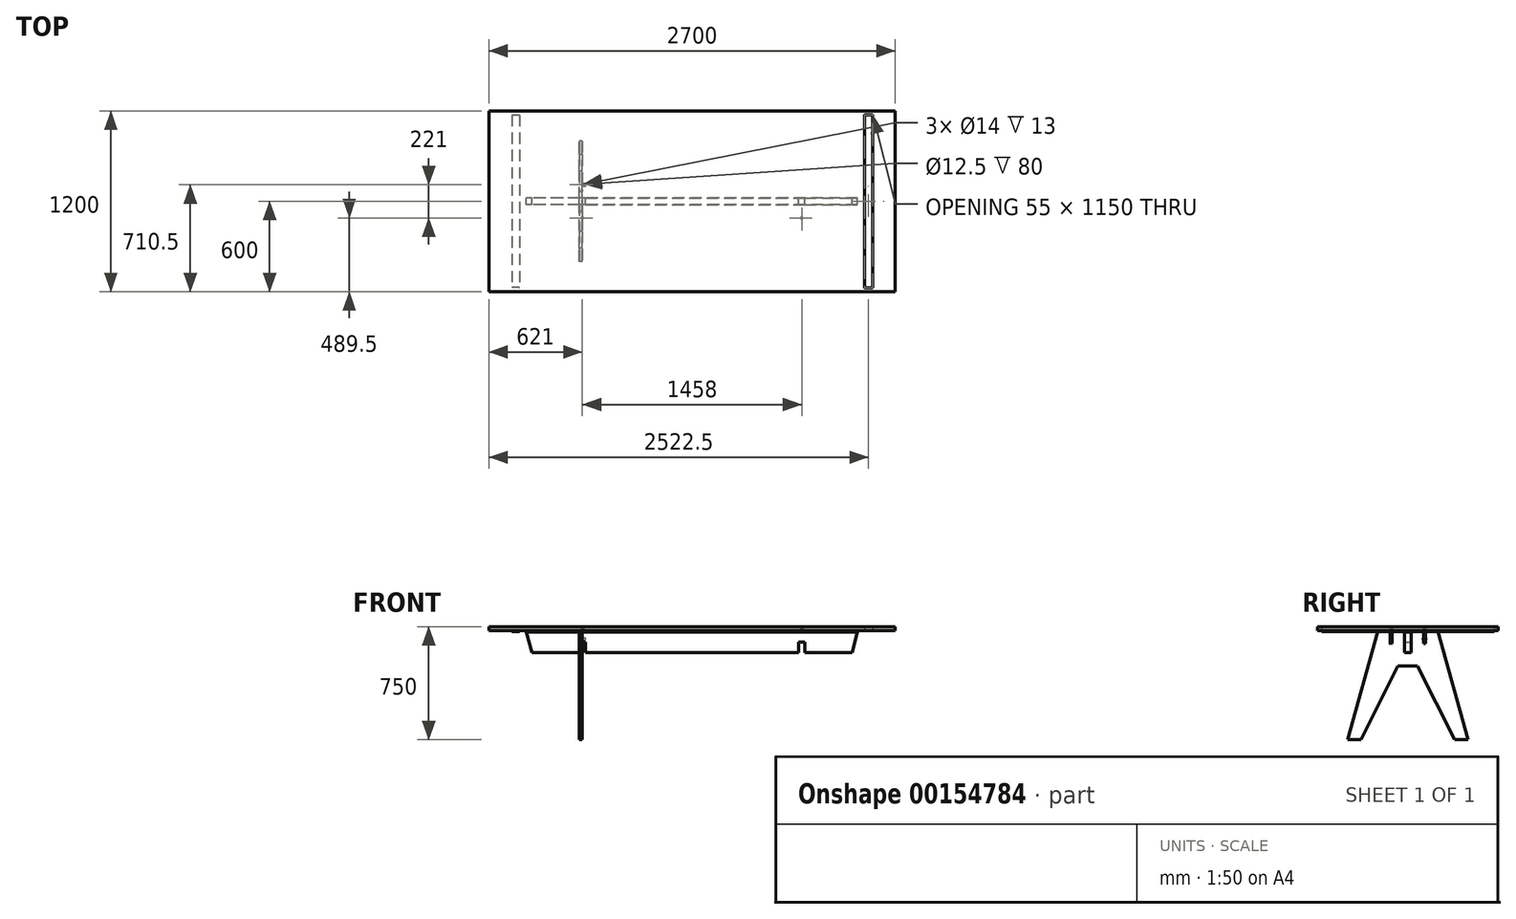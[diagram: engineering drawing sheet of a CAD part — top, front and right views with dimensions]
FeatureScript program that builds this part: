
annotation { "Feature Type Name" : "Feature", "Feature Type Description" : "" }
export const myFeature = defineFeature(function(context is Context, id is Id, definition is map)
    precondition{}
    {
        {
            var Q0;
            Q0=qCreatedBy(makeId("Top.planeOp"),FACE);
            var sketch = newSketch(context, id + "F0", { "sketchPlane" : qUnion([Q0])});
            skLineSegment(sketch, "E0.bottom", {"start": v(1350, 600) * mm, "end": v(-1350, 600) * mm});
            skLineSegment(sketch, "E0.top", {"start": v(1350, -600) * mm, "end": v(-1350, -600) * mm});
            skLineSegment(sketch, "E0.left", {"start": v(1350, 600) * mm, "end": v(1350, -600) * mm});
            skLineSegment(sketch, "E0.right", {"start": v(-1350, 600) * mm, "end": v(-1350, -600) * mm});
            skPoint(sketch, "E0.middle", {"position": v(0, 0) * mm});
            skLineSegment(sketch, "E1.bottom", {"start": v(-1148, 575) * mm, "end": v(-1197, 575) * mm});
            skLineSegment(sketch, "E1.top", {"start": v(-1148, -575) * mm, "end": v(-1197, -575) * mm});
            skLineSegment(sketch, "E1.left", {"start": v(-1145, 572) * mm, "end": v(-1145, -572) * mm});
            skLineSegment(sketch, "E1.right", {"start": v(-1200, 572) * mm, "end": v(-1200, -572) * mm});
            skPoint(sketch, "E1.middle", {"position": v(-1172.5, 0) * mm});
            skPoint(sketch, "E2.visualSharp", {"position": v(-1200, 575) * mm});
            skArc(sketch, "E2.filletArc", {"start": v(-1197, 575) * mm, "mid": v(-1199.12, 574.12) * mm, "end": v(-1200, 572) * mm});
            skPoint(sketch, "E3.visualSharp", {"position": v(-1145, 575) * mm});
            skArc(sketch, "E3.filletArc", {"start": v(-1145, 572) * mm, "mid": v(-1145.88, 574.12) * mm, "end": v(-1148, 575) * mm});
            skPoint(sketch, "E4.visualSharp", {"position": v(-1200, -575) * mm});
            skArc(sketch, "E4.filletArc", {"start": v(-1200, -572) * mm, "mid": v(-1199.12, -574.12) * mm, "end": v(-1197, -575) * mm});
            skPoint(sketch, "E5.visualSharp", {"position": v(-1145, -575) * mm});
            skArc(sketch, "E5.filletArc", {"start": v(-1148, -575) * mm, "mid": v(-1145.88, -574.12) * mm, "end": v(-1145, -572) * mm});
            skArc(sketch, "E6.MirrorCS", {"start": v(1148, -575) * mm, "mid": v(1145.88, -574.12) * mm, "end": v(1145, -572) * mm});
            skLineSegment(sketch, "E7.MirrorCS", {"start": v(1148, -575) * mm, "end": v(1197, -575) * mm});
            skArc(sketch, "E8.MirrorCS", {"start": v(1200, -572) * mm, "mid": v(1199.12, -574.12) * mm, "end": v(1197, -575) * mm});
            skLineSegment(sketch, "E9.MirrorCS", {"start": v(1148, 575) * mm, "end": v(1197, 575) * mm});
            skArc(sketch, "E10.MirrorCS", {"start": v(1197, 575) * mm, "mid": v(1199.12, 574.12) * mm, "end": v(1200, 572) * mm});
            skArc(sketch, "E11.MirrorCS", {"start": v(1145, 572) * mm, "mid": v(1145.88, 574.12) * mm, "end": v(1148, 575) * mm});
            skPoint(sketch, "E12.MirrorP", {"position": v(1172.5, 0) * mm});
            skLineSegment(sketch, "E13.MirrorCS", {"start": v(1145, 572) * mm, "end": v(1145, -572) * mm});
            skPoint(sketch, "E14.MirrorP", {"position": v(1145, -575) * mm});
            skLineSegment(sketch, "E15.MirrorCS", {"start": v(1200, 572) * mm, "end": v(1200, -572) * mm});
            skPoint(sketch, "E16.MirrorP", {"position": v(1200, -575) * mm});
            skArc(sketch, "E17.0", {"start": v(-1147.5, 572) * mm, "mid": v(-1147.65, 572.35) * mm, "end": v(-1148, 572.5) * mm});
            skLineSegment(sketch, "E17.1", {"start": v(-1148, 572.5) * mm, "end": v(-1197, 572.5) * mm});
            skLineSegment(sketch, "E17.2", {"start": v(-1147.5, 572) * mm, "end": v(-1147.5, -572) * mm});
            skArc(sketch, "E17.3", {"start": v(-1197, 572.5) * mm, "mid": v(-1197.35, 572.35) * mm, "end": v(-1197.5, 572) * mm});
            skArc(sketch, "E17.4", {"start": v(-1148, -572.5) * mm, "mid": v(-1147.65, -572.35) * mm, "end": v(-1147.5, -572) * mm});
            skLineSegment(sketch, "E17.5", {"start": v(-1148, -572.5) * mm, "end": v(-1197, -572.5) * mm});
            skArc(sketch, "E17.6", {"start": v(-1197.5, -572) * mm, "mid": v(-1197.35, -572.35) * mm, "end": v(-1197, -572.5) * mm});
            skLineSegment(sketch, "E17.7", {"start": v(-1197.5, 572) * mm, "end": v(-1197.5, -572) * mm});
            skSolve(sketch);
        }
        {
            var Q0;
            Q0=makeQuery(id+"F0.imprint","IMPRINT",FACE,{"disambiguationData":[TD([[makeQuery(id+"F0.imprint","IMPRINT",EDGE,{"derivedFrom":sQuery(id+"F0.wireOp",EDGE,"E1.bottom")}),1.0]])]});
            var Q1;
            Q1=makeQuery(id+"F0.imprint","IMPRINT",FACE,{"disambiguationData":[TD([[makeQuery(id+"F0.imprint","IMPRINT",EDGE,{"derivedFrom":sQuery(id+"F0.wireOp",EDGE,"E6.MirrorCS")}),-1.0]])]});
            var Q2;
            Q2=makeQuery(id+"F0.imprint","IMPRINT",FACE,{"disambiguationData":[TD([[makeQuery(id+"F0.imprint","IMPRINT",EDGE,{"derivedFrom":sQuery(id+"F0.wireOp",EDGE,"E0.bottom")}),1.0]])]});
            var Q3;
            Q3=makeQuery(id+"F0.imprint","IMPRINT",FACE,{"disambiguationData":[TD([[makeQuery(id+"F0.imprint","IMPRINT",EDGE,{"derivedFrom":sQuery(id+"F0.wireOp",EDGE,"E17.0")}),1.0]])]});
            extrude(context, id + "F1", {"entities" : qUnion([Q0, Q1, Q2, Q3]), "depth" : 32 * mm});
        }
        {
            var Q0;
            Q0=makeQuery(id+"F0.imprint","IMPRINT",FACE,{"disambiguationData":[TD([[makeQuery(id+"F0.imprint","IMPRINT",EDGE,{"derivedFrom":sQuery(id+"F0.wireOp",EDGE,"E1.bottom")}),1.0]])]});
            var Q1;
            Q1=makeQuery(id+"F0.imprint","IMPRINT",FACE,{"disambiguationData":[TD([[makeQuery(id+"F0.imprint","IMPRINT",EDGE,{"derivedFrom":sQuery(id+"F0.wireOp",EDGE,"E6.MirrorCS")}),-1.0]])]});
            var Q2;
            Q2=makeQuery(id+"F0.imprint","IMPRINT",FACE,{"disambiguationData":[TD([[makeQuery(id+"F0.imprint","IMPRINT",EDGE,{"derivedFrom":sQuery(id+"F0.wireOp",EDGE,"E17.0")}),1.0]])]});
            extrude(context, id + "F2", {"entities" : qUnion([Q0, Q1, Q2]), "operationType" : NewBodyOperationType.REMOVE, "depth" : 5 * mm});
        }
        {
            var Q0;
            Q0=makeQuery(id+"F0.imprint","IMPRINT",FACE,{"disambiguationData":[TD([[makeQuery(id+"F0.imprint","IMPRINT",EDGE,{"derivedFrom":sQuery(id+"F0.wireOp",EDGE,"E17.0")}),1.0]])]});
            extrude(context, id + "F3", {"entities" : qUnion([Q0]), "depth" : 5 * mm});
        }
        {
            var Q0;
            Q0=qCreatedBy(makeId("Right.planeOp"),FACE);
            cPlane(context, id + "F4", {"entities" : qUnion([Q0]), "cplaneType" : CPlaneType.OFFSET, "offset" : 750 * mm, "oppositeDirection" : true, "width" : 150 * mm, "height" : 150 * mm});
        }
        {
            var Q0;
            Q0=qCreatedBy(id+"F4.planeOp",FACE);
            var sketch = newSketch(context, id + "F5", { "sketchPlane" : qUnion([Q0])});
            skLineSegment(sketch, "E18", {"start": v(0, 0) * mm, "end": v(-200, 0) * mm});
            skLineSegment(sketch, "E19", {"start": v(-200, 0) * mm, "end": v(-400, -718) * mm});
            skLineSegment(sketch, "E20", {"start": v(-400, -718) * mm, "end": v(-310, -718) * mm});
            skLineSegment(sketch, "E21", {"start": v(-65, -228) * mm, "end": v(0, -228) * mm});
            skLineSegment(sketch, "E22.MirrorCS", {"start": v(400, -718) * mm, "end": v(310, -718) * mm});
            skLineSegment(sketch, "E23.MirrorCS", {"start": v(200, 0) * mm, "end": v(400, -718) * mm});
            skLineSegment(sketch, "E24.MirrorCS", {"start": v(0, 0) * mm, "end": v(200, 0) * mm});
            skLineSegment(sketch, "E25.bottom", {"start": v(-21, 0) * mm, "end": v(21, 0) * mm});
            skLineSegment(sketch, "E25.top", {"start": v(-21, -140) * mm, "end": v(21, -140) * mm});
            skLineSegment(sketch, "E25.left", {"start": v(-21, 0) * mm, "end": v(-21, -140) * mm});
            skLineSegment(sketch, "E25.right", {"start": v(21, 0) * mm, "end": v(21, -140) * mm});
            skPoint(sketch, "E25.middle", {"position": v(0, -70) * mm});
            skLineSegment(sketch, "E26", {"start": v(-310, -718) * mm, "end": v(-65, -228) * mm});
            skLineSegment(sketch, "E27.MirrorCS", {"start": v(310, -718) * mm, "end": v(65, -228) * mm});
            skLineSegment(sketch, "E28.MirrorCS", {"start": v(65, -228) * mm, "end": v(0, -228) * mm});
            skLineSegment(sketch, "E29", {"start": v(21, -70) * mm, "end": v(-21, -70) * mm});
            skSolve(sketch);
        }
        {
            var Q0;
            {var subQ5=sQuery(id+"F5.wireOp",EDGE,"E18");Q0=makeQuery(id+"F5.imprint","IMPRINT",FACE,{"disambiguationData":[TD([[makeQuery(id+"F5.imprint","IMPRINT",EDGE,{"derivedFrom":subQ5}),1.0]])]});}
            var Q1;
            {var subQ0=sQuery(id+"F5.wireOp",EDGE,"E25.top");Q1=makeQuery(id+"F5.imprint","IMPRINT",FACE,{"disambiguationData":[TD([[makeQuery(id+"F5.imprint","IMPRINT",EDGE,{"derivedFrom":subQ0}),1.0]])]});}
            extrude(context, id + "F6", {"entities" : qUnion([Q0, Q1]), "depth" : 42 * mm});
        }
        {
            var Q0;
            Q0=makeQuery(id+"F6.opExtrude","SWEPT_FACE",FACE,{"disambiguationData":[OSD([sQuery(id+"F5.wireOp",EDGE,"E24.MirrorCS")])]});
            var sketch = newSketch(context, id + "F7", { "sketchPlane" : qUnion([Q0])});
            skCircle(sketch, "E30", {"center": v(-729, 110.5) * mm, "radius": 7 * mm});
            skPoint(sketch, "E30.centerSnap0", {"position": v(-729, 200) * mm});
            skPoint(sketch, "E30.centerSnap1", {"position": v(-708, 110.5) * mm});
            skCircle(sketch, "E31", {"center": v(-729, 110.5) * mm, "radius": 6.25 * mm});
            skCircle(sketch, "E32.MirrorC", {"center": v(-729, -110.5) * mm, "radius": 7 * mm});
            skCircle(sketch, "E33.MirrorC", {"center": v(-729, -110.5) * mm, "radius": 6.25 * mm});
            skCircle(sketch, "E34.MirrorC", {"center": v(729, 110.5) * mm, "radius": 7 * mm});
            skCircle(sketch, "E35.MirrorC", {"center": v(729, -110.5) * mm, "radius": 7 * mm});
            skSolve(sketch);
        }
        {
            var Q0;
            Q0=makeQuery(id+"F7.imprint","IMPRINT",FACE,{"disambiguationData":[TD([[makeQuery(id+"F7.imprint","IMPRINT",EDGE,{"derivedFrom":sQuery(id+"F7.wireOp",EDGE,"E30")}),1.0]])]});
            var Q1;
            Q1=makeQuery(id+"F7.imprint","IMPRINT",FACE,{"disambiguationData":[TD([[makeQuery(id+"F7.imprint","IMPRINT",EDGE,{"derivedFrom":sQuery(id+"F7.wireOp",EDGE,"E31")}),1.0]])]});
            var Q2;
            Q2=makeQuery(id+"F7.imprint","IMPRINT",FACE,{"disambiguationData":[TD([[makeQuery(id+"F7.imprint","IMPRINT",EDGE,{"derivedFrom":sQuery(id+"F7.wireOp",EDGE,"E32.MirrorC")}),-1.0]])]});
            var Q3;
            Q3=makeQuery(id+"F7.imprint","IMPRINT",FACE,{"disambiguationData":[TD([[makeQuery(id+"F7.imprint","IMPRINT",EDGE,{"derivedFrom":sQuery(id+"F7.wireOp",EDGE,"E33.MirrorC")}),-1.0]])]});
            var Q4;
            Q4=makeQuery(id+"F7.imprint","IMPRINT",FACE,{"disambiguationData":[TD([[makeQuery(id+"F7.imprint","IMPRINT",EDGE,{"derivedFrom":sQuery(id+"F7.wireOp",EDGE,"E35.MirrorC")}),1.0]])]});
            var Q5;
            Q5=makeQuery(id+"F7.imprint","IMPRINT",FACE,{"disambiguationData":[TD([[makeQuery(id+"F7.imprint","IMPRINT",EDGE,{"derivedFrom":sQuery(id+"F7.wireOp",EDGE,"E34.MirrorC")}),-1.0]])]});
            extrude(context, id + "F8", {"entities" : qUnion([Q0, Q1, Q2, Q3, Q4, Q5]), "operationType" : NewBodyOperationType.REMOVE, "depth" : 18 * mm});
        }
        {
            var Q0;
            Q0=makeQuery(id+"F7.imprint","IMPRINT",FACE,{"disambiguationData":[TD([[makeQuery(id+"F7.imprint","IMPRINT",EDGE,{"derivedFrom":sQuery(id+"F7.wireOp",EDGE,"E31")}),1.0]])]});
            var Q1;
            Q1=makeQuery(id+"F7.imprint","IMPRINT",FACE,{"disambiguationData":[TD([[makeQuery(id+"F7.imprint","IMPRINT",EDGE,{"derivedFrom":sQuery(id+"F7.wireOp",EDGE,"E33.MirrorC")}),-1.0]])]});
            extrude(context, id + "F9", {"entities" : qUnion([Q0, Q1]), "operationType" : NewBodyOperationType.REMOVE, "oppositeDirection" : true, "depth" : 80 * mm});
        }
        {
            var Q0;
            Q0=makeQuery(id+"F6.opExtrude","CAP_FACE",FACE,{"disambiguationData":[OSD([sQuery(id+"F5.wireOp",EDGE,"E18"),sQuery(id+"F5.wireOp",EDGE,"E19"),sQuery(id+"F5.wireOp",EDGE,"E20"),sQuery(id+"F5.wireOp",EDGE,"E21"),sQuery(id+"F5.wireOp",EDGE,"E22.MirrorCS"),sQuery(id+"F5.wireOp",EDGE,"E23.MirrorCS"),sQuery(id+"F5.wireOp",EDGE,"E24.MirrorCS"),sQuery(id+"F5.wireOp",EDGE,"E25.left"),sQuery(id+"F5.wireOp",EDGE,"E25.right"),sQuery(id+"F5.wireOp",EDGE,"E26"),sQuery(id+"F5.wireOp",EDGE,"E27.MirrorCS"),sQuery(id+"F5.wireOp",EDGE,"E28.MirrorCS"),sQuery(id+"F5.wireOp",EDGE,"E29")])],"isStart":false});
            var sketch = newSketch(context, id + "F10", { "sketchPlane" : qUnion([Q0])});
            skLineSegment(sketch, "E36.0", {"start": v(-104.25, 0) * mm, "end": v(-116.75, 0) * mm, "construction": true});
            skCircle(sketch, "E37", {"center": v(-110.5, -50) * mm, "radius": 9 * mm});
            skPoint(sketch, "E37.centerSnap0", {"position": v(-110.5, 0) * mm});
            skCircle(sketch, "E38.MirrorC", {"center": v(110.5, -50) * mm, "radius": 9 * mm});
            skSolve(sketch);
        }
        {
            var Q0;
            Q0=makeQuery(id+"F10.imprint","IMPRINT",FACE,{"disambiguationData":[TD([[makeQuery(id+"F10.imprint","IMPRINT",EDGE,{"derivedFrom":sQuery(id+"F10.wireOp",EDGE,"E38.MirrorC")}),-1.0]])]});
            var Q1;
            Q1=makeQuery(id+"F10.imprint","IMPRINT",FACE,{"disambiguationData":[TD([[makeQuery(id+"F10.imprint","IMPRINT",EDGE,{"derivedFrom":sQuery(id+"F10.wireOp",EDGE,"E37")}),1.0]])]});
            extrude(context, id + "F11", {"entities" : qUnion([Q0, Q1]), "operationType" : NewBodyOperationType.REMOVE, "oppositeDirection" : true, "depth" : 23 * mm});
        }
        {
            var Q0;
            Q0=qCreatedBy(makeId("Front.planeOp"),FACE);
            var sketch = newSketch(context, id + "F12", { "sketchPlane" : qUnion([Q0])});
            skLineSegment(sketch, "E39.0", {"start": v(-708, -70) * mm, "end": v(-750, -70) * mm});
            skPoint(sketch, "E40.0", {"position": v(-750, -140) * mm});
            skLineSegment(sketch, "E41", {"start": v(-750, -140) * mm, "end": v(-750, -70) * mm});
            skLineSegment(sketch, "E42", {"start": v(-708, -70) * mm, "end": v(-708, -140) * mm});
            skLineSegment(sketch, "E43", {"start": v(-708, -140) * mm, "end": v(0, -140) * mm});
            skLineSegment(sketch, "E44", {"start": v(-750, -140) * mm, "end": v(-1063.02, -140) * mm});
            skLineSegment(sketch, "E45", {"start": v(-1063.02, -140) * mm, "end": v(-1100, -2) * mm});
            skLineSegment(sketch, "E46", {"start": v(-1100, -2) * mm, "end": v(0.37, -2) * mm});
            skLineSegment(sketch, "E47.MirrorCS", {"start": v(1100, -2) * mm, "end": v(-0.37, -2) * mm});
            skLineSegment(sketch, "E48.MirrorCS", {"start": v(1063.02, -140) * mm, "end": v(1100, -2) * mm});
            skLineSegment(sketch, "E49.MirrorCS", {"start": v(750, -140) * mm, "end": v(1063.02, -140) * mm});
            skLineSegment(sketch, "E50.MirrorCS", {"start": v(750, -140) * mm, "end": v(750, -70) * mm});
            skLineSegment(sketch, "E51.MirrorCS", {"start": v(708, -70) * mm, "end": v(750, -70) * mm});
            skLineSegment(sketch, "E52.MirrorCS", {"start": v(708, -70) * mm, "end": v(708, -140) * mm});
            skLineSegment(sketch, "E53.MirrorCS", {"start": v(708, -140) * mm, "end": v(0, -140) * mm});
            skSolve(sketch);
        }
        {
            var Q0;
            Q0=makeQuery(id+"F12.imprint","IMPRINT",FACE,{"disambiguationData":[TD([[makeQuery(id+"F12.imprint","IMPRINT",EDGE,{"derivedFrom":sQuery(id+"F12.wireOp",EDGE,"E39.0")}),-1.0]])]});
            extrude(context, id + "F13", {"entities" : qUnion([Q0]), "endBound" : BoundingType.SYMMETRIC, "depth" : 42 * mm});
        }
    });
